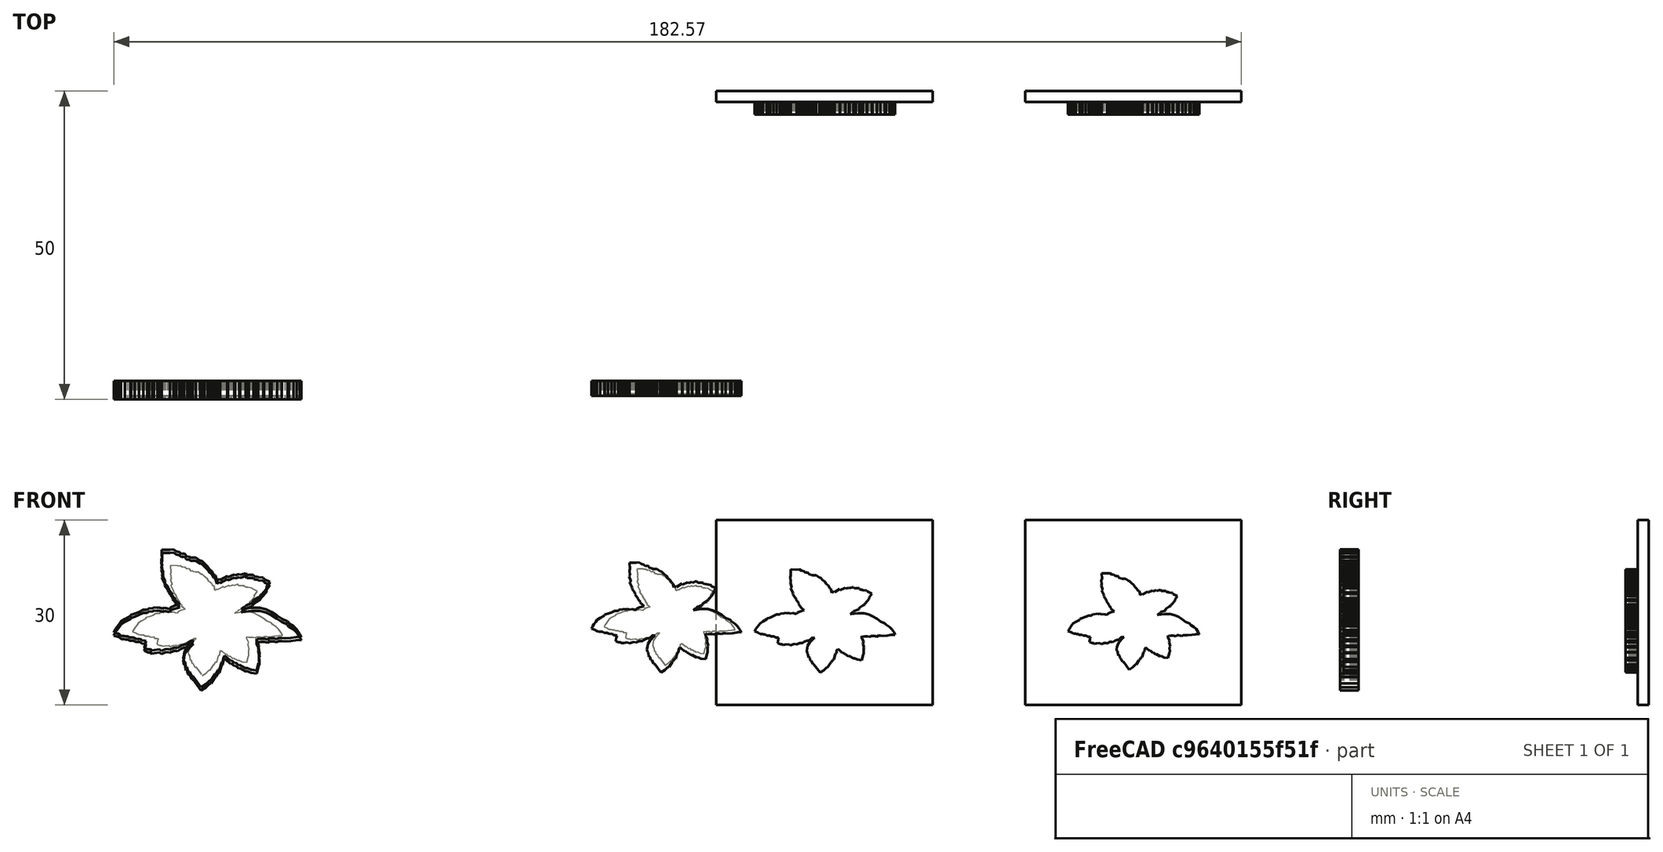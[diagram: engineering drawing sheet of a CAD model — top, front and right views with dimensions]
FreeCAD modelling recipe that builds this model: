
FCSTD DOCUMENT  (FreeCAD 0.20R29410 (Git))
Label: Logo
License: All rights reserved
LicenseURL: http://en.wikipedia.org/wiki/All_rights_reserved
objects: Part::Feature×6, App::MeasureDistance×3, Part::Box×2, Part::MultiFuse×2, Sketcher::SketchObject×1, PartDesign::Pad×1, PartDesign::Body×1, Part::FeaturePython×1
note: 15 computed .brp shape members not serialized (recipe doc carries the construction recipe); baked Part::Feature solids carry a one-line shape summary decoded from their .brp

FEATURE [Part::Box] Box068  label="logoBase001"
  AttacherType = Attacher::AttachEngine3D
  Height = 30
  Length = 35
  Placement = pos=(82.5,0,15.25) rot=(0,0,1;0rad)
  Width = 1.8
FEATURE [Sketcher::SketchObject] Sketch001
  FullyConstrained = false
  MapMode = 5
  Support = -> [XY_Plane001]
  sketch-geometry (205):
    g0: LineSegment StartX=-15.0667 StartY=-2.9879 StartZ=0 EndX=-14.4175 EndY=-3.20194 EndZ=0
    g1: LineSegment StartX=-14.1386 StartY=-3.3581 StartZ=0 EndX=-13.8673 EndY=-3.55064 EndZ=0
    g2: LineSegment StartX=-10.8098 StartY=-4.00788 StartZ=0 EndX=-10.5716 EndY=-4.29909 EndZ=0
    g3: LineSegment StartX=-10.5716 StartY=-4.29909 StartZ=0 EndX=-10.1338 EndY=-4.33136 EndZ=0
    g4: LineSegment StartX=-10.1338 StartY=-4.33136 StartZ=0 EndX=-9.89036 EndY=-4.3898 EndZ=0
    g5: LineSegment StartX=-9.51656 StartY=-5.73022 StartZ=0 EndX=-9.24931 EndY=-5.76229 EndZ=0
    g6: LineSegment StartX=-9.24931 StartY=-5.76229 StartZ=0 EndX=-8.92861 EndY=-5.90126 EndZ=0
    g7: LineSegment StartX=-8.92861 StartY=-5.90126 StartZ=0 EndX=-8.54378 EndY=-5.86384 EndZ=0
    g8: LineSegment StartX=-8.54378 StartY=-5.86384 StartZ=0 EndX=-7.71788 EndY=-5.75845 EndZ=0
    g9: LineSegment StartX=-7.71788 StartY=-5.75845 StartZ=0 EndX=-7.37291 EndY=-5.97257 EndZ=0
    g10: LineSegment StartX=-7.37291 StartY=-5.97257 StartZ=0 EndX=-6.72487 EndY=-5.72038 EndZ=0
    g11: LineSegment StartX=-6.72487 StartY=-5.72038 StartZ=0 EndX=-6.27066 EndY=-5.69481 EndZ=0
    g12: LineSegment StartX=-6.27066 StartY=-5.69481 StartZ=0 EndX=-6.06223 EndY=-5.80493 EndZ=0
    g13: LineSegment StartX=-6.06223 StartY=-5.80493 StartZ=0 EndX=-5.35089 EndY=-5.48914 EndZ=0
    g14: LineSegment StartX=-5.35089 StartY=-5.48914 StartZ=0 EndX=-5.02402 EndY=-5.48914 EndZ=0
    g15: LineSegment StartX=-5.02402 StartY=-5.48914 StartZ=0 EndX=-4.80126 EndY=-5.53132 EndZ=0
    g16: LineSegment StartX=-4.80126 StartY=-5.53132 StartZ=0 EndX=-4.19735 EndY=-5.16248 EndZ=0
    g17: LineSegment StartX=-3.75191 StartY=-4.97251 StartZ=0 EndX=-3.37714 EndY=-4.97251 EndZ=0
    g18: LineSegment StartX=-3.37714 StartY=-4.97251 StartZ=0 EndX=-2.81898 EndY=-4.45422 EndZ=0
    g19: LineSegment StartX=-2.81898 StartY=-4.45422 StartZ=0 EndX=-2.62761 EndY=-4.34259 EndZ=0
    g20: LineSegment StartX=-2.62761 StartY=-4.34259 StartZ=0 EndX=-2.15112 EndY=-4.35765 EndZ=0
    g21: LineSegment StartX=-2.38042 StartY=-4.51801 StartZ=0 EndX=-3.18577 EndY=-5.42702 EndZ=0
    g22: LineSegment StartX=-3.18577 StartY=-5.42702 StartZ=0 EndX=-3.61318 EndY=-6.05824 EndZ=0
    g23: LineSegment StartX=-3.61318 StartY=-6.05824 StartZ=0 EndX=-3.7111 EndY=-6.64579 EndZ=0
    g24: LineSegment StartX=-3.7111 StartY=-6.64579 StartZ=0 EndX=-3.83514 EndY=-7.15501 EndZ=0
    g25: LineSegment StartX=-3.83514 StartY=-7.15501 StartZ=0 EndX=-3.75878 EndY=-7.50876 EndZ=0
    g26: LineSegment StartX=-3.75878 StartY=-7.50876 StartZ=0 EndX=-3.70596 EndY=-7.68135 EndZ=0
    g27: LineSegment StartX=-3.70596 StartY=-7.68135 StartZ=0 EndX=-3.53967 EndY=-7.85202 EndZ=0
    g28: LineSegment StartX=-3.53967 StartY=-7.85202 StartZ=0 EndX=-3.4685 EndY=-8.65617 EndZ=0
    g29: LineSegment StartX=-3.27268 StartY=-8.56671 StartZ=0 EndX=-3.16823 EndY=-8.76909 EndZ=0
    g30: LineSegment StartX=-3.07088 StartY=-9.32083 StartZ=0 EndX=-2.84207 EndY=-9.3355 EndZ=0
    g31: LineSegment StartX=-2.84207 StartY=-9.3355 StartZ=0 EndX=-2.45193 EndY=-10.0982 EndZ=0
    g32: LineSegment StartX=-2.45193 StartY=-10.0982 StartZ=0 EndX=-2.24953 EndY=-10.1304 EndZ=0
    g33: LineSegment StartX=-2.24953 StartY=-10.1304 StartZ=0 EndX=-0.96042 EndY=-11.8753 EndZ=0
    g34: LineSegment StartX=-0.96042 StartY=-11.8753 StartZ=0 EndX=-0.153326 EndY=-11.3889 EndZ=0
    g35: LineSegment StartX=-0.153326 StartY=-11.3889 StartZ=0 EndX=0.461347 EndY=-10.7689 EndZ=0
    g36: LineSegment StartX=0.461347 StartY=-10.7689 StartZ=0 EndX=0.669802 EndY=-10.7261 EndZ=0
    g37: LineSegment StartX=0.669802 StartY=-10.7261 StartZ=0 EndX=1.31724 EndY=-9.70998 EndZ=0
    g38: LineSegment StartX=1.31724 StartY=-9.70998 StartZ=0 EndX=1.51826 EndY=-9.65081 EndZ=0
    g39: LineSegment StartX=1.51826 StartY=-9.65081 StartZ=0 EndX=1.74022 EndY=-9.08937 EndZ=0
    g40: LineSegment StartX=1.74022 StartY=-9.08937 StartZ=0 EndX=2.02094 EndY=-9.04367 EndZ=0
    g41: LineSegment StartX=2.02094 StartY=-9.04367 StartZ=0 EndX=2.39306 EndY=-7.80327 EndZ=0
    g42: LineSegment StartX=2.39306 StartY=-7.80327 StartZ=0 EndX=2.58839 EndY=-7.69871 EndZ=0
    g43: LineSegment StartX=2.6542 StartY=-7.03945 StartZ=0 EndX=2.86963 EndY=-6.81749 EndZ=0
    g44: LineSegment StartX=2.86963 StartY=-6.81749 StartZ=0 EndX=3.0916 EndY=-6.92847 EndZ=0
    g45: LineSegment StartX=3.0916 StartY=-6.92847 StartZ=0 EndX=3.79666 EndY=-7.57478 EndZ=0
    g46: LineSegment StartX=3.79666 StartY=-7.57478 StartZ=0 EndX=3.93376 EndY=-7.50297 EndZ=0
    g47: LineSegment StartX=3.93376 StartY=-7.50297 StartZ=0 EndX=4.46256 EndY=-7.97301 EndZ=0
    g48: LineSegment StartX=4.46256 StartY=-7.97301 StartZ=0 EndX=4.68452 EndY=-7.92079 EndZ=0
    g49: LineSegment StartX=4.68452 StartY=-7.92079 StartZ=0 EndX=5.1154 EndY=-8.34513 EndZ=0
    g50: LineSegment StartX=5.1154 StartY=-8.34513 StartZ=0 EndX=5.32431 EndY=-8.28637 EndZ=0
    g51: LineSegment StartX=5.32431 StartY=-8.28637 StartZ=0 EndX=6.23668 EndY=-8.79564 EndZ=0
    g52: LineSegment StartX=6.23668 StartY=-8.79564 StartZ=0 EndX=6.50362 EndY=-8.76631 EndZ=0
    g53: LineSegment StartX=6.50362 StartY=-8.76631 StartZ=0 EndX=7.14802 EndY=-9.05537 EndZ=0
    g54: LineSegment StartX=7.14802 StartY=-9.05537 StartZ=0 EndX=8.04883 EndY=-9.18613 EndZ=0
    g55: LineSegment StartX=8.04883 StartY=-9.18613 StartZ=0 EndX=8.36847 EndY=-7.93662 EndZ=0
    g56: LineSegment StartX=8.36847 StartY=-7.93662 StartZ=0 EndX=8.49923 EndY=-7.79133 EndZ=0
    g57: LineSegment StartX=8.49923 StartY=-7.79133 StartZ=0 EndX=8.43477 EndY=-6.72206 EndZ=0
    g58: LineSegment StartX=8.43477 StartY=-6.72206 StartZ=0 EndX=8.58621 EndY=-6.47988 EndZ=0
    g59: LineSegment StartX=8.58621 StartY=-6.47988 StartZ=0 EndX=8.32296 EndY=-5.53178 EndZ=0
    g60: LineSegment StartX=8.32296 StartY=-5.53178 StartZ=0 EndX=8.43984 EndY=-5.19091 EndZ=0
    g61: LineSegment StartX=8.43984 StartY=-5.19091 StartZ=0 EndX=8.07426 EndY=-4.39307 EndZ=0
    g62: LineSegment StartX=8.07426 StartY=-4.39307 StartZ=0 EndX=8.04236 EndY=-4.17777 EndZ=0
    g63: LineSegment StartX=8.04236 StartY=-4.17777 StartZ=0 EndX=8.0902 EndY=-3.99438 EndZ=0
    g64: LineSegment StartX=8.4103 StartY=-4.11103 StartZ=0 EndX=8.72013 EndY=-4.0502 EndZ=0
    g65: LineSegment StartX=8.72013 StartY=-4.0502 StartZ=0 EndX=9.31817 EndY=-4.0502 EndZ=0
    g66: LineSegment StartX=9.31817 StartY=-4.0502 StartZ=0 EndX=9.82964 EndY=-4.15887 EndZ=0
    g67: LineSegment StartX=10.1326 StartY=-3.9675 StartZ=0 EndX=10.5175 EndY=-3.9623 EndZ=0
    g68: LineSegment StartX=10.5175 StartY=-3.9623 StartZ=0 EndX=10.8831 EndY=-3.97536 EndZ=0
    g69: LineSegment StartX=10.8831 StartY=-3.97536 StartZ=0 EndX=11.2245 EndY=-4.09431 EndZ=0
    g70: LineSegment StartX=11.2245 StartY=-4.09431 StartZ=0 EndX=11.6861 EndY=-3.91007 EndZ=0
    g71: LineSegment StartX=11.6861 StartY=-3.91007 StartZ=0 EndX=12.1039 EndY=-3.88396 EndZ=0
    g72: LineSegment StartX=12.1039 StartY=-3.88396 StartZ=0 EndX=12.6 EndY=-3.9623 EndZ=0
    g73: LineSegment StartX=12.6 StartY=-3.9623 StartZ=0 EndX=13.5793 EndY=-3.87743 EndZ=0
    g74: LineSegment StartX=13.5793 StartY=-3.87743 StartZ=0 EndX=14.3888 EndY=-3.74687 EndZ=0
    g75: LineSegment StartX=14.3888 StartY=-3.74687 StartZ=0 EndX=14.7544 EndY=-3.68158 EndZ=0
    g76: LineSegment StartX=14.7544 StartY=-3.68158 StartZ=0 EndX=15.2767 EndY=-3.75339 EndZ=0
    g77: LineSegment StartX=15.2767 StartY=-3.75339 StartZ=0 EndX=15.0432 EndY=-3.24137 EndZ=0
    g78: LineSegment StartX=15.0432 StartY=-3.24137 StartZ=0 EndX=14.5209 EndY=-2.51672 EndZ=0
    g79: LineSegment StartX=14.5209 StartY=-2.51672 StartZ=0 EndX=14.0378 EndY=-1.99445 EndZ=0
    g80: LineSegment StartX=14.0378 StartY=-1.99445 StartZ=0 EndX=13.2802 EndY=-1.54625 EndZ=0
    g81: LineSegment StartX=13.2802 StartY=-1.54625 StartZ=0 EndX=13.0438 EndY=-1.23117 EndZ=0
    g82: LineSegment StartX=13.0438 StartY=-1.23117 StartZ=0 EndX=12.1074 EndY=-0.797939 EndZ=0
    g83: LineSegment StartX=12.1074 StartY=-0.797939 StartZ=0 EndX=11.3804 EndY=-0.250878 EndZ=0
    g84: LineSegment StartX=11.3804 StartY=-0.250878 StartZ=0 EndX=10.4396 EndY=0.304889 EndZ=0
    g85: LineSegment StartX=10.4396 StartY=0.304889 StartZ=0 EndX=9.59526 EndY=0.727998 EndZ=0
    g86: LineSegment StartX=9.59526 StartY=0.727998 StartZ=0 EndX=8.53624 EndY=0.97306 EndZ=0
    g87: LineSegment StartX=8.53624 StartY=0.97306 StartZ=0 EndX=7.199 EndY=0.97306 EndZ=0
    g88: LineSegment StartX=7.199 StartY=0.97306 StartZ=0 EndX=5.77932 EndY=0.795578 EndZ=0
    g89: LineSegment StartX=5.77932 StartY=0.795578 StartZ=0 EndX=5.60186 EndY=0.795578 EndZ=0
    g90: LineSegment StartX=5.60186 StartY=0.795578 StartZ=0 EndX=5.83178 EndY=0.981815 EndZ=0
    g91: LineSegment StartX=5.83178 StartY=0.981815 StartZ=0 EndX=6.25403 EndY=1.1582 EndZ=0
    g92: LineSegment StartX=6.30214 StartY=1.38269 StartZ=0 EndX=7.17987 EndY=1.70686 EndZ=0
    g93: LineSegment StartX=7.17987 StartY=1.70686 StartZ=0 EndX=7.44682 EndY=1.79438 EndZ=0
    g94: LineSegment StartX=7.44682 StartY=1.79438 StartZ=0 EndX=7.49058 EndY=2.12696 EndZ=0
    g95: LineSegment StartX=7.49058 StartY=2.12696 StartZ=0 EndX=8.30058 EndY=2.66839 EndZ=0
    g96: LineSegment StartX=8.30058 StartY=2.66839 StartZ=0 EndX=8.68575 EndY=2.81854 EndZ=0
    g97: LineSegment StartX=8.68575 StartY=2.81854 StartZ=0 EndX=8.68575 EndY=3.12537 EndZ=0
    g98: LineSegment StartX=8.68575 StartY=3.12537 StartZ=0 EndX=8.89508 EndY=3.18684 EndZ=0
    g99: LineSegment StartX=8.89508 StartY=3.18684 StartZ=0 EndX=9.63492 EndY=4.06602 EndZ=0
    g100: LineSegment StartX=9.63492 StartY=4.06602 StartZ=0 EndX=9.62638 EndY=4.32743 EndZ=0
    g101: LineSegment StartX=9.62638 StartY=4.32743 StartZ=0 EndX=10.2068 EndY=5.18314 EndZ=0
    g102: LineSegment StartX=10.2068 StartY=5.18314 StartZ=0 EndX=9.25518 EndY=5.64445 EndZ=0
    g103: LineSegment StartX=9.1102 StartY=5.87597 StartZ=0 EndX=8.32132 EndY=5.97336 EndZ=0
    g104: LineSegment StartX=8.32132 StartY=5.97336 StartZ=0 EndX=8.15466 EndY=6.06625 EndZ=0
    g105: LineSegment StartX=7.63471 StartY=6.13088 StartZ=0 EndX=7.56391 EndY=6.33267 EndZ=0
    g106: LineSegment StartX=7.56391 StartY=6.33267 StartZ=0 EndX=6.74832 EndY=6.35496 EndZ=0
    g107: LineSegment StartX=6.74832 StartY=6.35496 StartZ=0 EndX=6.46819 EndY=6.29526 EndZ=0
    g108: LineSegment StartX=6.46819 StartY=6.29526 StartZ=0 EndX=6.27042 EndY=6.61061 EndZ=0
    g109: LineSegment StartX=6.27042 StartY=6.61061 StartZ=0 EndX=5.40453 EndY=6.33267 EndZ=0
    g110: LineSegment StartX=5.40453 StartY=6.33267 StartZ=0 EndX=5.27091 EndY=6.47164 EndZ=0
    g111: LineSegment StartX=5.27091 StartY=6.47164 StartZ=0 EndX=4.56942 EndY=6.24725 EndZ=0
    g112: LineSegment StartX=4.56942 StartY=6.24725 StartZ=0 EndX=4.44161 EndY=6.40652 EndZ=0
    g113: LineSegment StartX=4.44161 StartY=6.40652 StartZ=0 EndX=3.4195 EndY=5.94588 EndZ=0
    g114: LineSegment StartX=3.4195 StartY=5.94588 StartZ=0 EndX=3.29192 EndY=6.1532 EndZ=0
    g115: LineSegment StartX=3.29192 StartY=6.1532 StartZ=0 EndX=2.15964 EndY=5.49137 EndZ=0
    g116: LineSegment StartX=2.15964 StartY=5.49137 StartZ=0 EndX=2.00016 EndY=5.69869 EndZ=0
    g117: LineSegment StartX=2.00016 StartY=5.69869 StartZ=0 EndX=1.6185 EndY=5.34828 EndZ=0
    g118: LineSegment StartX=1.6185 StartY=5.34828 StartZ=0 EndX=1.45984 EndY=5.94974 EndZ=0
    g119: LineSegment StartX=1.38165 StartY=6.28651 StartZ=0 EndX=1.14534 EndY=6.29963 EndZ=0
    g120: LineSegment StartX=0.348522 StartY=7.29544 StartZ=0 EndX=0.126706 EndY=7.68126 EndZ=0
    g121: LineSegment StartX=0.126706 StartY=7.68126 StartZ=0 EndX=-0.415308 EndY=8.18163 EndZ=0
    g122: LineSegment StartX=-0.415308 StartY=8.18163 StartZ=0 EndX=-0.872658 EndY=8.6237 EndZ=0
    g123: LineSegment StartX=-0.872658 StartY=8.6237 StartZ=0 EndX=-1.12074 EndY=8.64329 EndZ=0
    g124: LineSegment StartX=-1.12074 StartY=8.64329 StartZ=0 EndX=-1.79316 EndY=9.11986 EndZ=0
    g125: LineSegment StartX=-1.79316 StartY=9.11986 StartZ=0 EndX=-2.31488 EndY=9.12122 EndZ=0
    g126: LineSegment StartX=-2.31488 StartY=9.12122 StartZ=0 EndX=-2.71321 EndY=9.13846 EndZ=0
    g127: LineSegment StartX=-2.71321 StartY=9.13846 StartZ=0 EndX=-2.88425 EndY=9.34157 EndZ=0
    g128: LineSegment StartX=-2.88425 StartY=9.34157 StartZ=0 EndX=-3.16779 EndY=9.26454 EndZ=0
    g129: LineSegment StartX=-3.70739 StartY=9.82796 StartZ=0 EndX=-4.04915 EndY=9.7003 EndZ=0
    g130: LineSegment StartX=-4.04915 StartY=9.7003 StartZ=0 EndX=-4.42988 EndY=10.011 EndZ=0
    g131: LineSegment StartX=-5.98947 StartY=10.3656 StartZ=0 EndX=-7.32605 EndY=10.4108 EndZ=0
    g132: LineSegment StartX=-7.25254 StartY=9.13254 StartZ=0 EndX=-7.36878 EndY=8.7693 EndZ=0
    g133: LineSegment StartX=-7.36878 StartY=8.7693 StartZ=0 EndX=-7.2614 EndY=7.83762 EndZ=0
    g134: LineSegment StartX=-7.2614 StartY=7.83762 StartZ=0 EndX=-7.41112 EndY=7.6042 EndZ=0
    g135: LineSegment StartX=-7.41112 StartY=7.6042 StartZ=0 EndX=-7.09216 EndY=6.74302 EndZ=0
    g136: LineSegment StartX=-7.09216 StartY=6.74302 StartZ=0 EndX=-7.10014 EndY=6.55962 EndZ=0
    g137: LineSegment StartX=-7.10014 StartY=6.55962 StartZ=0 EndX=-7.29151 EndY=6.3842 EndZ=0
    g138: LineSegment StartX=-7.29151 StartY=6.3842 StartZ=0 EndX=-6.74132 EndY=5.29976 EndZ=0
    g139: LineSegment StartX=-6.74132 StartY=5.29976 StartZ=0 EndX=-6.87495 EndY=5.02732 EndZ=0
    g140: LineSegment StartX=-6.87495 StartY=5.02732 StartZ=0 EndX=-6.31586 EndY=4.42065 EndZ=0
    g141: LineSegment StartX=-6.31586 StartY=4.42065 StartZ=0 EndX=-6.30396 EndY=4.19463 EndZ=0
    g142: LineSegment StartX=-6.30396 StartY=4.19463 StartZ=0 EndX=-6.05415 EndY=4.0043 EndZ=0
    g143: LineSegment StartX=-6.05415 StartY=4.0043 StartZ=0 EndX=-6.18501 EndY=3.95672 EndZ=0
    g144: LineSegment StartX=-6.18501 StartY=3.95672 StartZ=0 EndX=-5.54265 EndY=3.07645 EndZ=0
    g145: LineSegment StartX=-5.54265 StartY=3.07645 StartZ=0 EndX=-5.57833 EndY=2.90991 EndZ=0
    g146: LineSegment StartX=-5.57833 StartY=2.90991 StartZ=0 EndX=-5.1263 EndY=2.41029 EndZ=0
    g147: LineSegment StartX=-5.1263 StartY=2.41029 StartZ=0 EndX=-5.18578 EndY=2.26755 EndZ=0
    g148: LineSegment StartX=-5.18578 StartY=2.26755 StartZ=0 EndX=-4.73375 EndY=1.89878 EndZ=0
    g149: LineSegment StartX=-4.73375 StartY=1.89878 StartZ=0 EndX=-4.42446 EndY=1.5895 EndZ=0
    g150: LineSegment StartX=-4.42446 StartY=1.5895 StartZ=0 EndX=-5.31663 EndY=1.29211 EndZ=0
    g151: LineSegment StartX=-5.31663 StartY=1.29211 StartZ=0 EndX=-5.84004 EndY=1.08988 EndZ=0
    g152: LineSegment StartX=-5.84004 StartY=1.08988 StartZ=0 EndX=-6.04226 EndY=0.792495 EndZ=0
    g153: LineSegment StartX=-6.04226 StartY=0.792495 StartZ=0 EndX=-6.94632 EndY=0.994719 EndZ=0
    g154: LineSegment StartX=-6.94632 StartY=0.994719 StartZ=0 EndX=-7.19613 EndY=0.887659 EndZ=0
    g155: LineSegment StartX=-7.19613 StartY=0.887659 StartZ=0 EndX=-7.8147 EndY=1.0423 EndZ=0
    g156: LineSegment StartX=-7.8147 StartY=1.0423 StartZ=0 EndX=-8.02502 EndY=0.969153 EndZ=0
    g157: LineSegment StartX=-8.02502 StartY=0.969153 StartZ=0 EndX=-8.60267 EndY=1.03042 EndZ=0
    g158: LineSegment StartX=-8.60267 StartY=1.03042 StartZ=0 EndX=-8.8346 EndY=0.872878 EndZ=0
    g159: LineSegment StartX=-8.8346 StartY=0.872878 StartZ=0 EndX=-9.33349 EndY=0.929767 EndZ=0
    g160: LineSegment StartX=-9.33349 StartY=0.929767 StartZ=0 EndX=-9.66169 EndY=0.649695 EndZ=0
    g161: LineSegment StartX=-9.66169 StartY=0.649695 StartZ=0 EndX=-10.3249 EndY=0.649695 EndZ=0
    g162: LineSegment StartX=-10.3249 StartY=0.649695 StartZ=0 EndX=-11.0107 EndY=0.32425 EndZ=0
    g163: LineSegment StartX=-11.0107 StartY=0.32425 StartZ=0 EndX=-11.7283 EndY=0.053139 EndZ=0
    g164: LineSegment StartX=-11.7283 StartY=0.053139 StartZ=0 EndX=-12.2971 EndY=-0.13161 EndZ=0
    g165: LineSegment StartX=-12.2971 StartY=-0.13161 StartZ=0 EndX=-12.4212 EndY=-0.347049 EndZ=0
    g166: LineSegment StartX=-12.4212 StartY=-0.347049 StartZ=0 EndX=-13.296 EndY=-0.817096 EndZ=0
    g167: LineSegment StartX=-13.296 StartY=-0.817096 StartZ=0 EndX=-13.9227 EndY=-1.24144 EndZ=0
    g168: LineSegment StartX=-13.9227 StartY=-1.24144 StartZ=0 EndX=-14.1708 EndY=-1.59398 EndZ=0
    g169: LineSegment StartX=-14.1708 StartY=-1.59398 StartZ=0 EndX=-14.5386 EndY=-2.09216 EndZ=0
    g170: LineSegment StartX=-14.5386 StartY=-2.09216 StartZ=0 EndX=-14.7831 EndY=-2.4577 EndZ=0
    g171: LineSegment StartX=-14.7831 StartY=-2.4577 StartZ=0 EndX=-15.0667 EndY=-2.9879 EndZ=0
    g172: LineSegment StartX=7.82861 StartY=6.04487 StartZ=0 EndX=7.63471 EndY=6.13088 EndZ=0
    g173: LineSegment StartX=-14.4175 StartY=-3.20194 StartZ=0 EndX=-14.1386 EndY=-3.3581 EndZ=0
    g174: LineSegment StartX=-13.8673 StartY=-3.55064 StartZ=0 EndX=-13.4107 EndY=-3.57136 EndZ=0
    g175: LineSegment StartX=-13.1321 StartY=-3.61699 StartZ=0 EndX=-12.817 EndY=-3.62343 EndZ=0
    g176: LineSegment StartX=-12.817 StartY=-3.62343 StartZ=0 EndX=-12.4662 EndY=-3.85302 EndZ=0
    g177: LineSegment StartX=-13.4107 StartY=-3.57136 StartZ=0 EndX=-13.1321 EndY=-3.61699 EndZ=0
    g178: LineSegment StartX=-12.4662 StartY=-3.85302 StartZ=0 EndX=-11.8704 EndY=-3.85302 EndZ=0
    g179: LineSegment StartX=-11.8704 StartY=-3.85302 StartZ=0 EndX=-11.5204 EndY=-4.00836 EndZ=0
    g180: LineSegment StartX=-11.5204 StartY=-4.00836 StartZ=0 EndX=-11.1389 EndY=-4.05555 EndZ=0
    g181: LineSegment StartX=-11.1389 StartY=-4.05555 StartZ=0 EndX=-10.8098 EndY=-4.00788 EndZ=0
    g182: LineSegment StartX=-9.89036 StartY=-4.3898 StartZ=0 EndX=-9.99555 EndY=-4.87697 EndZ=0
    g183: LineSegment StartX=-9.99555 StartY=-4.87697 StartZ=0 EndX=-10.0894 EndY=-5.36391 EndZ=0
    g184: LineSegment StartX=-10.0894 StartY=-5.36391 StartZ=0 EndX=-10.107 EndY=-5.50471 EndZ=0
    g185: LineSegment StartX=-10.107 StartY=-5.50471 StartZ=0 EndX=-9.77848 EndY=-5.63965 EndZ=0
    g186: LineSegment StartX=-9.77848 StartY=-5.63965 StartZ=0 EndX=-9.51656 EndY=-5.73022 EndZ=0
    g187: LineSegment StartX=-4.19735 StartY=-5.16248 StartZ=0 EndX=-3.75191 EndY=-4.97251 EndZ=0
    g188: LineSegment StartX=-2.38042 StartY=-4.51801 StartZ=0 EndX=-2.15112 EndY=-4.35765 EndZ=0
    g189: LineSegment StartX=-3.4685 StartY=-8.65617 StartZ=0 EndX=-3.27268 EndY=-8.56671 EndZ=0
    g190: LineSegment StartX=-3.16823 StartY=-8.76909 StartZ=0 EndX=-3.07088 EndY=-9.32083 EndZ=0
    g191: LineSegment StartX=2.58839 StartY=-7.69871 StartZ=0 EndX=2.6542 EndY=-7.03945 EndZ=0
    g192: LineSegment StartX=8.0902 StartY=-3.99438 StartZ=0 EndX=8.4103 EndY=-4.11103 EndZ=0
    g193: LineSegment StartX=9.82964 StartY=-4.15887 StartZ=0 EndX=10.1326 EndY=-3.9675 EndZ=0
    g194: LineSegment StartX=6.30214 StartY=1.38269 StartZ=0 EndX=6.25403 EndY=1.1582 EndZ=0
    g195: LineSegment StartX=1.38165 StartY=6.28651 StartZ=0 EndX=1.45984 EndY=5.94974 EndZ=0
    g196: LineSegment StartX=0.348522 StartY=7.29544 StartZ=0 EndX=0.824344 EndY=6.91479 EndZ=0
    g197: LineSegment StartX=0.824344 StartY=6.91479 StartZ=0 EndX=1.14534 EndY=6.29963 EndZ=0
    g198: LineSegment StartX=-3.70739 StartY=9.82796 StartZ=0 EndX=-3.16779 EndY=9.26454 EndZ=0
    g199: LineSegment StartX=-5.98947 StartY=10.3656 StartZ=0 EndX=-5.43038 EndY=10.4489 EndZ=0
    g200: LineSegment StartX=-5.43038 StartY=10.4489 StartZ=0 EndX=-4.9791 EndY=10.1425 EndZ=0
    g201: LineSegment StartX=-4.42988 StartY=10.011 StartZ=0 EndX=-4.9791 EndY=10.1425 EndZ=0
    g202: LineSegment StartX=-7.25254 StartY=9.13254 StartZ=0 EndX=-7.32605 EndY=10.4108 EndZ=0
    g203: LineSegment StartX=7.82861 StartY=6.04487 StartZ=0 EndX=8.15466 EndY=6.06625 EndZ=0
    g204: LineSegment StartX=9.1102 StartY=5.87597 StartZ=0 EndX=9.25518 EndY=5.64445 EndZ=0
  constraints (114):
    c: Coincident(g4,g3)
    c: Coincident(g6,g5)
    c: Coincident(g8,g7)
    c: Coincident(g9,g8)
    c: Coincident(g10,g9)
    c: Coincident(g11,g10)
    c: Coincident(g13,g12)
    c: Coincident(g16,g15)
    c: Coincident(g22,g21)
    c: Coincident(g25,g24)
    c: Coincident(g26,g25)
    c: Coincident(g28,g27)
    c: Coincident(g33,g32)
    c: Coincident(g37,g36)
    c: Coincident(g38,g37)
    c: Coincident(g40,g39)
    c: Coincident(g44,g43)
    c: Coincident(g51,g50)
    c: Coincident(g52,g51)
    c: Coincident(g57,g56)
    c: Coincident(g58,g57)
    c: Coincident(g59,g58)
    c: Coincident(g61,g60)
    c: Coincident(g63,g62)
    c: Coincident(g66,g65)
    c: Coincident(g70,g69)
    c: Coincident(g72,g71)
    c: Coincident(g73,g72)
    c: Coincident(g74,g73)
    c: Coincident(g77,g76)
    c: Coincident(g80,g79)
    c: Coincident(g81,g80)
    c: Coincident(g83,g82)
    c: Coincident(g85,g84)
    c: Coincident(g86,g85)
    c: Coincident(g87,g86)
    c: Coincident(g89,g88)
    c: Coincident(g90,g89)
    c: Coincident(g91,g90)
    c: Coincident(g93,g92)
    c: Coincident(g95,g94)
    c: Coincident(g97,g96)
    c: Coincident(g98,g97)
    c: Coincident(g99,g98)
    c: Coincident(g100,g99)
    c: Coincident(g104,g103)
    c: Coincident(g106,g105)
    c: Coincident(g107,g106)
    c: Coincident(g111,g110)
    c: Coincident(g113,g112)
    c: Coincident(g118,g117)
    c: Coincident(g122,g121)
    c: Coincident(g126,g125)
    c: Coincident(g130,g129)
    c: Coincident(g133,g132)
    c: Coincident(g134,g133)
    c: Coincident(g135,g134)
    c: Coincident(g139,g138)
    c: Coincident(g142,g141)
    c: Coincident(g156,g155)
    c: Coincident(g157,g156)
    c: Coincident(g159,g158)
    c: Coincident(g161,g160)
    c: Coincident(g164,g163)
    c: Coincident(g165,g164)
    c: Coincident(g168,g167)
    c: Coincident(g169,g168)
    c: Coincident(g171,g170)
    c: Coincident(g171,g0)
    c: Coincident(g172,g105)
    c: DistanceX(g165) = -12.4212
    c: DistanceY(g165) = -0.347049
    c: Coincident(g173,g0)
    c: Coincident(g173,g1)
    c: Coincident(g174,g1)
    c: Coincident(g177,g174)
    c: Coincident(g177,g175)
    c: Coincident(g178,g176)
    c: Coincident(g181,g2)
    c: Coincident(g182,g4)
    c: Coincident(g186,g185)
    c: Coincident(g186,g5)
    c: Coincident(g187,g16)
    c: Coincident(g187,g17)
    c: Coincident(g188,g21)
    c: Coincident(g188,g20)
    c: Coincident(g189,g28)
    c: Coincident(g189,g29)
    c: Coincident(g190,g29)
    c: Coincident(g190,g30)
    c: Coincident(g191,g42)
    c: Coincident(g191,g43)
    c: Coincident(g192,g63)
    c: Coincident(g192,g64)
    c: Coincident(g193,g66)
    c: Coincident(g193,g67)
    c: Coincident(g194,g92)
    c: Coincident(g194,g91)
    c: Coincident(g195,g119)
    c: Coincident(g195,g118)
    c: Coincident(g196,g120)
    c: Coincident(g197,g119)
    c: Coincident(g198,g129)
    c: Coincident(g198,g128)
    c: Coincident(g199,g131)
    c: Coincident(g200,g199)
    c: Coincident(g201,g130)
    c: Coincident(g201,g200)
    c: Coincident(g202,g132)
    c: Coincident(g202,g131)
    c: Coincident(g203,g172)
    c: Coincident(g203,g104)
    c: Coincident(g204,g103)
    c: Coincident(g204,g102)
FEATURE [PartDesign::Pad] Pad001
  Direction = (0,0,1)
  Length = 3
  Length2 = 10
  Profile = -> Sketch001
  ReferenceAxis = -> Sketch001 [N_Axis]
  Type = 0
FEATURE [PartDesign::Body] Body001  label="logo002"
  Group = -> [Sketch001,Pad001]
  Origin = -> Origin001
  Placement = pos=(39.35,-43,30) rot=(1,0,0;1.5708rad)
  Tip = -> Pad001
FEATURE [Part::FeaturePython] Clone  label="logo003"  # Draft clone (typed FeaturePython)
  AttacherType = Attacher::AttachEngine3D
  Fuse = false
  Objects = -> [Body001]
  Placement = pos=(74.85,-45.2,30) rot=(1,0,0;1.5708rad)
  Scale = (0.7,0.7,0.7)
FEATURE [Part::Box] Box069  label="logoBase002"
  AttacherType = Attacher::AttachEngine3D
  Height = 30
  Length = 35
  Placement = pos=(132.5,0,15.25) rot=(0,0,1;0rad)
  Width = 1.8
FEATURE [Part::Feature] Clone005  label="logo004"
  Placement = pos=(74.3,-45.2,30) rot=(1,0,0;1.5708rad)
  shape: bbox 24.27 x 2.4 x 17.86 mm, 207 faces (baked)
FEATURE [Part::Feature] Clone006  label="logo100"
  Placement = pos=(0,-45.2,30) rot=(1,0,0;1.5708rad)
  shape: bbox 30.34 x 3 x 22.32 mm, 207 faces (baked)
FEATURE [Part::Feature] Clone007  label="logo090"
  Placement = pos=(0,-45.2,29.5) rot=(1,0,0;1.5708rad)
  shape: bbox 30.34 x 3 x 22.32 mm, 207 faces (baked)
FEATURE [Part::Feature] Clone008  label="logo080"
  Placement = pos=(0,-45.2,29.5) rot=(1,0,0;1.5708rad)
  shape: bbox 24.27 x 2.4 x 17.86 mm, 207 faces (baked)
FEATURE [Part::Feature] Clone009  label="logo075"
  Placement = pos=(100,0.25,29.4) rot=(1,0,0;1.5708rad)
  shape: bbox 22.76 x 2.25 x 16.74 mm, 207 faces (baked)
FEATURE [Part::Feature] Clone010  label="logo070"
  Placement = pos=(150,0.1,29.3) rot=(1,0,0;1.5708rad)
  shape: bbox 21.24 x 2.1 x 15.63 mm, 207 faces (baked)
FEATURE [Part::MultiFuse] Fusion  label="logo75"
  Shapes = -> [Clone009,Box068]
FEATURE [Part::MultiFuse] Fusion001  label="logo70"
  Shapes = -> [Clone010,Box069]
FEATURE [App::MeasureDistance] Distance  label="Distance: 1.80 mm"
  Distance = 1.8
  P1 = (82.5,1.8,45.25)
  P2 = (82.5,0,45.25)
FEATURE [App::MeasureDistance] Distance001  label="Distance: 18.10 mm"
  Distance = 18.0967
  P1 = (88.6688,0,45.25)
  P2 = (88.7563,-2,27.2644)
FEATURE [App::MeasureDistance] Distance002  label="Distance: 1.99 mm"
  Distance = 1.99083
  P1 = (139.453,-0.00917147,27.2085)
  P2 = (139.453,-2,27.2085)
